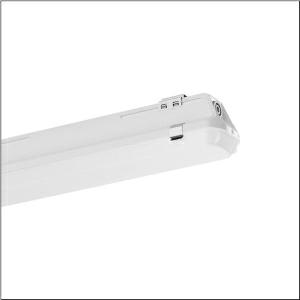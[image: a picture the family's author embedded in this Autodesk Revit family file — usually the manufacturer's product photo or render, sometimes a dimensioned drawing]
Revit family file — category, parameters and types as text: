
# Revit family: monsun_r__21_parking_51fg207p440b_4b42
name_source: partatom
category: Lighting Fixtures
units: mm (PartAtom-declared; Revit-internal decimal feet)

## family parameters
Cut with Voids When Loaded = No
Host = Face
Light Source = No
Part Type = Normal
Room Calculation Point = No
Round Connector Dimension = Use Diameter
Shared = No

## types (1)
- Monsun® 21 parking (1 x LED, 5050 lm, 35.4 W, 4000K)
    Apparent Load = 35 VA
    CIE Flux Codes = 45 75 93 94 100
    Color Rendering = 80
    Color Temperature = 4000K
    Default Elevation = 1800 mm
    Description = Monsun® 21 parking, damp-proof luminaire, chain hanger, primary optical cover: enclosure, of PC, light emission: direct distribution, primary light characteristic: symmetric, installation type: suspended mounting, surface-mounted, horizontal mounting, vertical mounting, LED, rated luminous flux: 5.050lm, luminous efficacy: 143lm/W, light colour: 840, colour temperature: 4000K, control gear: ECG, with terminal, 3-pole, max. 2.5mm², mains connection: 220..240V, AC, 50/60Hz, rated input power: 35W, housing, of glass-fibre reinforced polyester, uncoated, bright grey, incl. chain hanger, length: 1.590mm, width: 90mm, height: 88mm, clip for enclosure, of stainless steel (V2A), ceiling mounting element, of stainless steel (V2A), chain hanger, of stainless steel (V2A), protection rating (complete): IP66, insulation class (complete): insulation class I (protective earthing), certification: CE, ENEC, VDE, UKCA, protection symbol: D, impact resistance: IK08, permissible operating ambient temperature: -25..+35°C, standard: EN 50419, EN 60598-2-1, corresponds to IFS (International Featured Standards) requirements for safety and quality in the food industry, for indoor or canopied outdoor use, no direct snow, no direct sun, no direct rain, contact your sales advisor before using the luminaires in applications with unclear chemical exposure, large temperature fluctuations or condensation-forming humidity, LABS conformity tested according to VDMA 24364:2018-05, packaging unit: 1 piece
    Height = 89 mm
    Lamp = 1 x LED
    Lamp Light Flux = 5050 lm
    Lamp Power = 35.4 W
    Lamp count = 1
    Length = 1590 mm
    Luminous efficacy = 143 lm/W
    Manufacturer = Siteco
    ModVariant = No
    Model = 51FG207P440B
    Mounting Place = Ceiling
    Mounting Type = Surface mounted
    Number of Poles = 1
    OnlyDefault = Yes
    Power Factor = 1
    Product Name = Monsun® 21 parking
    Product group = damp-proof luminaire
    ProductGroupID = 300
    Protection Class = Protection class I
    Protection Degree = IP 66
    RLX_Detail_Level = 1
    RLX_Emergency_Light_Flux = 0 lm
    RLX_Emergency_Type = 0
    RLX_Emergency_Type_DB = No
    RlxData = <blob elided: 88413 chars, md5=002a0a70>
    Socket = socket
    Standby Power = 0 W
    System Light Flux = 5050 lm
    System Power = 35 W
    Type Comments = Product without accessories
    Type Image = l_1319656.jpg
    URL = http://relux.com
    VarID = ---
    Voltage = 0 V
    Weight = 0.00 kg
    Width = 90 mm

## geometry (parser evidence)
native form markers: Blend x4, Sweep x13
no freeform markers — native parametric forms only
